# Revit family: 926-10-001-DN50-500
name_source: partatom
category: Pipe Accessories
units: mm (PartAtom-declared; Revit-internal decimal feet)

## family parameters
Always vertical = Yes
Cut with Voids When Loaded = No
Part Type = Valve - Breaks Into
Round Connector Dimension = Use Diameter
Shared = No
Work Plane-Based = No

## types (18) — shared parameters
DN050_PN 10/16 = 926-050-10-020140100000
DN080_PN 10/16 = 926-080-10-020140100000
DN100_PN 10/16 = 926-100-10-020140100000
DN150_PN 10/16 = 926-150-10-020040100000
DN200_PN 10 = 926-200-10-010040100000
DN200_PN 16 = 926-200-10-020040100000
DN250_PN 10 = 926-250-10-010040100000
DN250_PN 16 = 926-250-10-020040100000
DN300_PN 10 = 926-300-10-010040100000
DN300_PN 16 = 926-300-10-020040100000
DN350_PN 10 = 926-350-10-010040100000
DN350_PN 16 = 926-350-10-020040100000
DN400_PN 10 = 926-400-10-010040100000
DN400_PN 16 = 926-400-10-020040100000
DN450_PN 10 = 926-450-10-010040100000
DN450_PN 16 = 926-450-10-020040100000
DN500_PN 10 = 926-500-10-010040100000
DN500_PN 16 = 926-500-10-020040100000
Search_table = 926-10-001-DN50-500
URL_product_pages = https://www.avkvalves.com
zero-valued in all types: Default Elevation

## per-type parameters (varying)
- DN500_PN 16: A=130 mm; B=380 mm; Body_T=15 mm  [stored 0.0492126 ft]; Body_end_shaft_R=58 mm; Body_rib_L=87 mm; Body_rib_W=38 mm  [stored 0.124672 ft]; Body_shaft_R1=51 mm; Body_shaft_R2=44 mm; Body_shaft_R2_T=37 mm; Body_shaft_R3=57 mm; Body_shaft_R3_T=20 mm  [stored 0.0656168 ft]; Bore_R=250 mm; C=511 mm; D=46 mm; DN=500 mm; Description_=AVK DBL. ECC. BUTTERFLY VALVE, WAFER; E=65 mm; FL_R=285 mm; FL_T=22 mm  [stored 0.0721785 ft]; Hole_R=16 mm  [stored 0.0524934 ft]; L=6 mm  [stored 0.019685 ft]; PCD=650 mm; Raised_R=260 mm; Raised_dis=4 mm  [stored 0.0131234 ft]; Rib_R=23 mm  [stored 0.0754593 ft]; Rib_T=12 mm  [stored 0.0393701 ft]; Seal_R=18 mm  [stored 0.0590551 ft]; Slot_T=29 mm; Slot_dim1=12 mm  [stored 0.0393701 ft]; Top _Flange_dim1=38 mm  [stored 0.124672 ft]; Top _Flange_dim2=40 mm  [stored 0.131234 ft]; Top_Flange_R=105 mm; Top_Rib=23 mm  [stored 0.0754593 ft]; Wedge=100 mm; bottom_Shaft_R=59 mm; bottom_Shaft_T=27 mm  [stored 0.0885827 ft]; logo=267 mm; rib_Loctn=35 mm  [stored 0.114829 ft]; total_FL_legth=124 mm
- DN500_PN 10: A=130 mm; B=380 mm; Body_T=15 mm  [stored 0.0492126 ft]; Body_end_shaft_R=58 mm; Body_rib_L=87 mm; Body_rib_W=38 mm  [stored 0.124672 ft]; Body_shaft_R1=53 mm; Body_shaft_R2=44 mm; Body_shaft_R2_T=37 mm; Body_shaft_R3=57 mm; Body_shaft_R3_T=20 mm  [stored 0.0656168 ft]; Bore_R=250 mm; C=511 mm; D=46 mm; DN=500 mm; Description_=AVK DBL. ECC. BUTTERFLY VALVE, WAFER; E=65 mm; FL_R=285 mm; FL_T=19 mm  [stored 0.062336 ft]; Hole_R=16 mm  [stored 0.0524934 ft]; L=6 mm  [stored 0.019685 ft]; PCD=620 mm; Raised_R=260 mm; Raised_dis=4 mm  [stored 0.0131234 ft]; Rib_R=23 mm  [stored 0.0754593 ft]; Rib_T=10 mm  [stored 0.0328084 ft]; Seal_R=18 mm  [stored 0.0590551 ft]; Slot_T=29 mm; Slot_dim1=12 mm  [stored 0.0393701 ft]; Top _Flange_dim1=38 mm  [stored 0.124672 ft]; Top _Flange_dim2=40 mm  [stored 0.131234 ft]; Top_Flange_R=105 mm; Top_Rib=23 mm  [stored 0.0754593 ft]; Wedge=100 mm; bottom_Shaft_R=59 mm; bottom_Shaft_T=27 mm  [stored 0.0885827 ft]; logo=267 mm; rib_Loctn=35 mm  [stored 0.114829 ft]; total_FL_legth=124 mm
- DN450_PN 16: A=117 mm; B=360 mm; Body_T=16 mm  [stored 0.0524934 ft]; Body_end_shaft_R=52 mm; Body_rib_L=78 mm; Body_rib_W=41 mm  [stored 0.134514 ft]; Body_shaft_R1=45 mm; Body_shaft_R2=39 mm  [stored 0.127953 ft]; Body_shaft_R2_T=29 mm; Body_shaft_R3=51 mm; Body_shaft_R3_T=16 mm  [stored 0.0524934 ft]; Bore_R=225 mm; C=492 mm; D=36 mm  [stored 0.11811 ft]; DN=450 mm; Description_=AVK DBL. ECC. BUTTERFLY VALVE, WAFER; E=38 mm  [stored 0.124672 ft]; FL_R=265 mm; FL_T=22 mm  [stored 0.0721785 ft]; Hole_R=15 mm  [stored 0.0492126 ft]; L=6 mm  [stored 0.019685 ft]; PCD=585 mm; Raised_R=245 mm; Raised_dis=4 mm  [stored 0.0131234 ft]; Rib_R=18 mm  [stored 0.0590551 ft]; Rib_T=12 mm  [stored 0.0393701 ft]; Seal_R=20 mm  [stored 0.0656168 ft]; Slot_T=23 mm  [stored 0.0754593 ft]; Slot_dim1=10 mm  [stored 0.0328084 ft]; Top _Flange_dim1=34 mm  [stored 0.111549 ft]; Top _Flange_dim2=31 mm  [stored 0.101706 ft]; Top_Flange_R=105 mm; Top_Rib=18 mm  [stored 0.0590551 ft]; Wedge=90 mm; bottom_Shaft_R=53 mm; bottom_Shaft_T=29 mm; logo=243 mm; rib_Loctn=31 mm  [stored 0.101706 ft]; total_FL_legth=111 mm
- DN450_PN 10: A=117 mm; B=360 mm; Body_T=16 mm  [stored 0.0524934 ft]; Body_end_shaft_R=52 mm; Body_rib_L=78 mm; Body_rib_W=41 mm  [stored 0.134514 ft]; Body_shaft_R1=46 mm; Body_shaft_R2=39 mm  [stored 0.127953 ft]; Body_shaft_R2_T=29 mm; Body_shaft_R3=51 mm; Body_shaft_R3_T=16 mm  [stored 0.0524934 ft]; Bore_R=225 mm; C=492 mm; D=36 mm  [stored 0.11811 ft]; DN=450 mm; Description_=AVK DBL. ECC. BUTTERFLY VALVE, WAFER; E=38 mm  [stored 0.124672 ft]; FL_R=265 mm; FL_T=19 mm  [stored 0.062336 ft]; Hole_R=15 mm  [stored 0.0492126 ft]; L=6 mm  [stored 0.019685 ft]; PCD=565 mm; Raised_R=245 mm; Raised_dis=4 mm  [stored 0.0131234 ft]; Rib_R=18 mm  [stored 0.0590551 ft]; Rib_T=10 mm  [stored 0.0328084 ft]; Seal_R=20 mm  [stored 0.0656168 ft]; Slot_T=23 mm  [stored 0.0754593 ft]; Slot_dim1=10 mm  [stored 0.0328084 ft]; Top _Flange_dim1=34 mm  [stored 0.111549 ft]; Top _Flange_dim2=31 mm  [stored 0.101706 ft]; Top_Flange_R=105 mm; Top_Rib=18 mm  [stored 0.0590551 ft]; Wedge=90 mm; bottom_Shaft_R=53 mm; bottom_Shaft_T=29 mm; logo=243 mm; rib_Loctn=31 mm  [stored 0.101706 ft]; total_FL_legth=111 mm
- DN400_PN 16: A=105 mm; B=350 mm; Body_T=15 mm  [stored 0.0492126 ft]; Body_end_shaft_R=46 mm; Body_rib_L=70 mm; Body_rib_W=42 mm; Body_shaft_R1=39 mm  [stored 0.127953 ft]; Body_shaft_R2=35 mm  [stored 0.114829 ft]; Body_shaft_R2_T=29 mm; Body_shaft_R3=46 mm; Body_shaft_R3_T=16 mm  [stored 0.0524934 ft]; Bore_R=200 mm; C=451 mm; D=36 mm  [stored 0.11811 ft]; DN=400 mm; Description_=AVK DBL. ECC. BUTTERFLY VALVE, WAFER; E=41 mm  [stored 0.134514 ft]; FL_R=240 mm; FL_T=22 mm  [stored 0.0721785 ft]; Hole_R=14 mm  [stored 0.0459318 ft]; L=6 mm  [stored 0.019685 ft]; PCD=525 mm; Raised_R=220 mm; Raised_dis=4 mm  [stored 0.0131234 ft]; Rib_R=18 mm  [stored 0.0590551 ft]; Rib_T=12 mm  [stored 0.0393701 ft]; Seal_R=20 mm  [stored 0.0656168 ft]; Slot_T=23 mm  [stored 0.0754593 ft]; Slot_dim1=10 mm  [stored 0.0328084 ft]; Top _Flange_dim1=31 mm  [stored 0.101706 ft]; Top _Flange_dim2=31 mm  [stored 0.101706 ft]; Top_Flange_R=88 mm; Top_Rib=18 mm  [stored 0.0590551 ft]; Wedge=81 mm; bottom_Shaft_R=48 mm; bottom_Shaft_T=29 mm; logo=217 mm; rib_Loctn=28 mm  [stored 0.0918635 ft]; total_FL_legth=99 mm
- DN400_PN 10: A=51 mm; B=110 mm; Body_T=8 mm  [stored 0.0262467 ft]; Body_end_shaft_R=22 mm  [stored 0.0721785 ft]; Body_rib_L=20 mm  [stored 0.0656168 ft]; Body_rib_W=12 mm  [stored 0.0393701 ft]; Body_shaft_R1=19 mm  [stored 0.062336 ft]; Body_shaft_R2=10 mm  [stored 0.0328084 ft]; Body_shaft_R2_T=7 mm  [stored 0.0229659 ft]; Body_shaft_R3=13 mm; Body_shaft_R3_T=4 mm  [stored 0.0131234 ft]; Bore_R=40 mm  [stored 0.131234 ft]; C=185 mm; D=9 mm  [stored 0.0295276 ft]; DN=80 mm; Description_=AVK DBL. ECC. BUTTERFLY VALVE, WAFER AWWA SHORT, PN10/16; E=18 mm  [stored 0.0590551 ft]; FL_R=75 mm; FL_T=10 mm  [stored 0.0328084 ft]; Hole_R=5 mm  [stored 0.0164042 ft]; L=3 mm  [stored 0.00984252 ft]; PCD=160 mm; Raised_R=64 mm; Raised_dis=2 mm  [stored 0.00656168 ft]; Rib_R=5 mm  [stored 0.0164042 ft]; Rib_T=5 mm  [stored 0.0164042 ft]; Seal_R=18 mm  [stored 0.0590551 ft]; Slot_T=6 mm  [stored 0.019685 ft]; Slot_dim1=2 mm  [stored 0.00656168 ft]; Top _Flange_dim1=9 mm  [stored 0.0295276 ft]; Top _Flange_dim2=8 mm  [stored 0.0262467 ft]; Top_Flange_R=45 mm; Top_Rib=5 mm  [stored 0.0164042 ft]; Wedge=39 mm  [stored 0.127953 ft]; bottom_Shaft_R=14 mm  [stored 0.0459318 ft]; bottom_Shaft_T=8 mm  [stored 0.0262467 ft]; logo=50 mm; rib_Loctn=8 mm  [stored 0.0262467 ft]; total_FL_legth=48 mm
- DN350_PN 16: A=96 mm; B=290 mm; Body_T=14 mm  [stored 0.0459318 ft]; Body_end_shaft_R=43 mm; Body_rib_L=67 mm; Body_rib_W=31 mm  [stored 0.101706 ft]; Body_shaft_R1=36 mm  [stored 0.11811 ft]; Body_shaft_R2=34 mm  [stored 0.111549 ft]; Body_shaft_R2_T=29 mm; Body_shaft_R3=44 mm; Body_shaft_R3_T=16 mm  [stored 0.0524934 ft]; Bore_R=175 mm; C=420 mm; D=36 mm  [stored 0.11811 ft]; DN=350 mm; Description_=AVK DBL. ECC. BUTTERFLY VALVE, WAFER; E=41 mm  [stored 0.134514 ft]; FL_R=210 mm; FL_T=20 mm  [stored 0.0656168 ft]; Hole_R=13 mm; L=5 mm  [stored 0.0164042 ft]; PCD=470 mm; Raised_R=190 mm; Raised_dis=3 mm  [stored 0.00984252 ft]; Rib_R=18 mm  [stored 0.0590551 ft]; Rib_T=11 mm  [stored 0.0360892 ft]; Seal_R=18 mm  [stored 0.0590551 ft]; Slot_T=23 mm  [stored 0.0754593 ft]; Slot_dim1=10 mm  [stored 0.0328084 ft]; Top _Flange_dim1=30 mm  [stored 0.0984252 ft]; Top _Flange_dim2=31 mm  [stored 0.101706 ft]; Top_Flange_R=75 mm; Top_Rib=18 mm  [stored 0.0590551 ft]; Wedge=74 mm; bottom_Shaft_R=46 mm; bottom_Shaft_T=22 mm  [stored 0.0721785 ft]; logo=191 mm; rib_Loctn=27 mm  [stored 0.0885827 ft]; total_FL_legth=92 mm
- DN350_PN 10: A=96 mm; B=290 mm; Body_T=14 mm  [stored 0.0459318 ft]; Body_end_shaft_R=43 mm; Body_rib_L=67 mm; Body_rib_W=31 mm  [stored 0.101706 ft]; Body_shaft_R1=37 mm; Body_shaft_R2=34 mm  [stored 0.111549 ft]; Body_shaft_R2_T=29 mm; Body_shaft_R3=44 mm; Body_shaft_R3_T=16 mm  [stored 0.0524934 ft]; Bore_R=175 mm; C=420 mm; D=36 mm  [stored 0.11811 ft]; DN=350 mm; Description_=AVK DBL. ECC. BUTTERFLY VALVE, WAFER; E=41 mm  [stored 0.134514 ft]; FL_R=210 mm; FL_T=18 mm  [stored 0.0590551 ft]; Hole_R=13 mm; L=5 mm  [stored 0.0164042 ft]; PCD=460 mm; Raised_R=190 mm; Raised_dis=3 mm  [stored 0.00984252 ft]; Rib_R=18 mm  [stored 0.0590551 ft]; Rib_T=10 mm  [stored 0.0328084 ft]; Seal_R=18 mm  [stored 0.0590551 ft]; Slot_T=23 mm  [stored 0.0754593 ft]; Slot_dim1=10 mm  [stored 0.0328084 ft]; Top _Flange_dim1=30 mm  [stored 0.0984252 ft]; Top _Flange_dim2=31 mm  [stored 0.101706 ft]; Top_Flange_R=75 mm; Top_Rib=18 mm  [stored 0.0590551 ft]; Wedge=74 mm; bottom_Shaft_R=46 mm; bottom_Shaft_T=22 mm  [stored 0.0721785 ft]; logo=191 mm; rib_Loctn=27 mm  [stored 0.0885827 ft]; total_FL_legth=92 mm
- DN300_PN 16: A=86 mm; B=260 mm; Body_T=14 mm  [stored 0.0459318 ft]; Body_end_shaft_R=38 mm  [stored 0.124672 ft]; Body_rib_L=60 mm; Body_rib_W=30 mm  [stored 0.0984252 ft]; Body_shaft_R1=32 mm  [stored 0.104987 ft]; Body_shaft_R2=30 mm  [stored 0.0984252 ft]; Body_shaft_R2_T=22 mm  [stored 0.0721785 ft]; Body_shaft_R3=39 mm  [stored 0.127953 ft]; Body_shaft_R3_T=12 mm  [stored 0.0393701 ft]; Bore_R=150 mm; C=390 mm; D=27 mm  [stored 0.0885827 ft]; DN=300 mm; Description_=AVK DBL. ECC. BUTTERFLY VALVE, WAFER; E=41 mm  [stored 0.134514 ft]; FL_R=180 mm; FL_T=18 mm  [stored 0.0590551 ft]; Hole_R=12 mm  [stored 0.0393701 ft]; L=5 mm  [stored 0.0164042 ft]; PCD=410 mm; Raised_R=160 mm; Raised_dis=3 mm  [stored 0.00984252 ft]; Rib_R=14 mm  [stored 0.0459318 ft]; Rib_T=10 mm  [stored 0.0328084 ft]; Seal_R=15 mm  [stored 0.0492126 ft]; Slot_T=17 mm  [stored 0.0557743 ft]; Slot_dim1=7 mm  [stored 0.0229659 ft]; Top _Flange_dim1=27 mm  [stored 0.0885827 ft]; Top _Flange_dim2=23 mm  [stored 0.0754593 ft]; Top_Flange_R=75 mm; Top_Rib=14 mm  [stored 0.0459318 ft]; Wedge=66 mm; bottom_Shaft_R=41 mm  [stored 0.134514 ft]; bottom_Shaft_T=21 mm  [stored 0.0688976 ft]; logo=166 mm; rib_Loctn=24 mm  [stored 0.0787402 ft]; total_FL_legth=81 mm
- DN300_PN 10: A=86 mm; B=260 mm; Body_T=14 mm  [stored 0.0459318 ft]; Body_end_shaft_R=38 mm  [stored 0.124672 ft]; Body_rib_L=60 mm; Body_rib_W=30 mm  [stored 0.0984252 ft]; Body_shaft_R1=32 mm  [stored 0.104987 ft]; Body_shaft_R2=30 mm  [stored 0.0984252 ft]; Body_shaft_R2_T=22 mm  [stored 0.0721785 ft]; Body_shaft_R3=39 mm  [stored 0.127953 ft]; Body_shaft_R3_T=12 mm  [stored 0.0393701 ft]; Bore_R=150 mm; C=390 mm; D=27 mm  [stored 0.0885827 ft]; DN=300 mm; Description_=AVK DBL. ECC. BUTTERFLY VALVE, WAFER; E=41 mm  [stored 0.134514 ft]; FL_R=180 mm; FL_T=18 mm  [stored 0.0590551 ft]; Hole_R=12 mm  [stored 0.0393701 ft]; L=5 mm  [stored 0.0164042 ft]; PCD=400 mm; Raised_R=160 mm; Raised_dis=3 mm  [stored 0.00984252 ft]; Rib_R=14 mm  [stored 0.0459318 ft]; Rib_T=10 mm  [stored 0.0328084 ft]; Seal_R=15 mm  [stored 0.0492126 ft]; Slot_T=17 mm  [stored 0.0557743 ft]; Slot_dim1=7 mm  [stored 0.0229659 ft]; Top _Flange_dim1=27 mm  [stored 0.0885827 ft]; Top _Flange_dim2=23 mm  [stored 0.0754593 ft]; Top_Flange_R=75 mm; Top_Rib=14 mm  [stored 0.0459318 ft]; Wedge=66 mm; bottom_Shaft_R=41 mm  [stored 0.134514 ft]; bottom_Shaft_T=21 mm  [stored 0.0688976 ft]; logo=166 mm; rib_Loctn=24 mm  [stored 0.0787402 ft]; total_FL_legth=81 mm
- DN250_PN 16: A=79 mm; B=222 mm; Body_T=4 mm  [stored 0.0131234 ft]; Body_end_shaft_R=36 mm  [stored 0.11811 ft]; Body_rib_L=56 mm; Body_rib_W=24 mm  [stored 0.0787402 ft]; Body_shaft_R1=29 mm; Body_shaft_R2=28 mm  [stored 0.0918635 ft]; Body_shaft_R2_T=22 mm  [stored 0.0721785 ft]; Body_shaft_R3=36 mm  [stored 0.11811 ft]; Body_shaft_R3_T=12 mm  [stored 0.0393701 ft]; Bore_R=125 mm; C=340 mm; D=27 mm  [stored 0.0885827 ft]; DN=250 mm; Description_=AVK DBL. ECC. BUTTERFLY VALVE, WAFER; E=36 mm  [stored 0.11811 ft]; FL_R=160 mm; FL_T=18 mm  [stored 0.0590551 ft]; Hole_R=11 mm  [stored 0.0360892 ft]; L=3 mm  [stored 0.00984252 ft]; PCD=350 mm; Raised_R=140 mm; Raised_dis=2 mm  [stored 0.00656168 ft]; Rib_R=14 mm  [stored 0.0459318 ft]; Rib_T=11 mm  [stored 0.0360892 ft]; Seal_R=18 mm  [stored 0.0590551 ft]; Slot_T=17 mm  [stored 0.0557743 ft]; Slot_dim1=7 mm  [stored 0.0229659 ft]; Top _Flange_dim1=25 mm  [stored 0.082021 ft]; Top _Flange_dim2=23 mm  [stored 0.0754593 ft]; Top_Flange_R=75 mm; Top_Rib=14 mm  [stored 0.0459318 ft]; Wedge=61 mm; bottom_Shaft_R=38 mm  [stored 0.124672 ft]; bottom_Shaft_T=17 mm  [stored 0.0557743 ft]; logo=131 mm; rib_Loctn=22 mm  [stored 0.0721785 ft]; total_FL_legth=76 mm
- DN250_PN 10: A=79 mm; B=222 mm; Body_T=14 mm  [stored 0.0459318 ft]; Body_end_shaft_R=36 mm  [stored 0.11811 ft]; Body_rib_L=56 mm; Body_rib_W=24 mm  [stored 0.0787402 ft]; Body_shaft_R1=29 mm; Body_shaft_R2=28 mm  [stored 0.0918635 ft]; Body_shaft_R2_T=22 mm  [stored 0.0721785 ft]; Body_shaft_R3=36 mm  [stored 0.11811 ft]; Body_shaft_R3_T=12 mm  [stored 0.0393701 ft]; Bore_R=125 mm; C=340 mm; D=27 mm  [stored 0.0885827 ft]; DN=250 mm; Description_=AVK DBL. ECC. BUTTERFLY VALVE, WAFER; E=36 mm  [stored 0.11811 ft]; FL_R=160 mm; FL_T=18 mm  [stored 0.0590551 ft]; Hole_R=11 mm  [stored 0.0360892 ft]; L=3 mm  [stored 0.00984252 ft]; PCD=350 mm; Raised_R=140 mm; Raised_dis=2 mm  [stored 0.00656168 ft]; Rib_R=14 mm  [stored 0.0459318 ft]; Rib_T=11 mm  [stored 0.0360892 ft]; Seal_R=18 mm  [stored 0.0590551 ft]; Slot_T=17 mm  [stored 0.0557743 ft]; Slot_dim1=7 mm  [stored 0.0229659 ft]; Top _Flange_dim1=25 mm  [stored 0.082021 ft]; Top _Flange_dim2=23 mm  [stored 0.0754593 ft]; Top_Flange_R=75 mm; Top_Rib=14 mm  [stored 0.0459318 ft]; Wedge=61 mm; bottom_Shaft_R=38 mm  [stored 0.124672 ft]; bottom_Shaft_T=17 mm  [stored 0.0557743 ft]; logo=141 mm; rib_Loctn=22 mm  [stored 0.0721785 ft]; total_FL_legth=76 mm
- DN200_PN 16: A=75 mm; B=200 mm; Body_T=14 mm  [stored 0.0459318 ft]; Body_end_shaft_R=34 mm  [stored 0.111549 ft]; Body_rib_L=52 mm; Body_rib_W=22 mm  [stored 0.0721785 ft]; Body_shaft_R1=27 mm  [stored 0.0885827 ft]; Body_shaft_R2=26 mm; Body_shaft_R2_T=18 mm  [stored 0.0590551 ft]; Body_shaft_R3=34 mm  [stored 0.111549 ft]; Body_shaft_R3_T=10 mm  [stored 0.0328084 ft]; Bore_R=100 mm; C=320 mm; D=22 mm  [stored 0.0721785 ft]; DN=200 mm; Description_=AVK DBL. ECC. BUTTERFLY VALVE, WAFER; E=30 mm  [stored 0.0984252 ft]; FL_R=130 mm; FL_T=17 mm  [stored 0.0557743 ft]; Hole_R=10 mm  [stored 0.0328084 ft]; L=3 mm  [stored 0.00984252 ft]; PCD=295 mm; Raised_R=110 mm; Raised_dis=2 mm  [stored 0.00656168 ft]; Rib_R=11 mm  [stored 0.0360892 ft]; Rib_T=10 mm  [stored 0.0328084 ft]; Seal_R=15 mm  [stored 0.0492126 ft]; Slot_T=14 mm  [stored 0.0459318 ft]; Slot_dim1=6 mm  [stored 0.019685 ft]; Top _Flange_dim1=23 mm  [stored 0.0754593 ft]; Top _Flange_dim2=19 mm  [stored 0.062336 ft]; Top_Flange_R=63 mm; Top_Rib=11 mm  [stored 0.0360892 ft]; Wedge=57 mm; bottom_Shaft_R=35 mm  [stored 0.114829 ft]; bottom_Shaft_T=15 mm  [stored 0.0492126 ft]; logo=116 mm; rib_Loctn=21 mm  [stored 0.0688976 ft]; total_FL_legth=72 mm
- DN200_PN 10: A=75 mm; B=200 mm; Body_T=12 mm  [stored 0.0393701 ft]; Body_end_shaft_R=34 mm  [stored 0.111549 ft]; Body_rib_L=52 mm; Body_rib_W=22 mm  [stored 0.0721785 ft]; Body_shaft_R1=28 mm  [stored 0.0918635 ft]; Body_shaft_R2=26 mm; Body_shaft_R2_T=18 mm  [stored 0.0590551 ft]; Body_shaft_R3=34 mm  [stored 0.111549 ft]; Body_shaft_R3_T=10 mm  [stored 0.0328084 ft]; Bore_R=100 mm; C=320 mm; D=22 mm  [stored 0.0721785 ft]; DN=200 mm; Description_=AVK DBL. ECC. BUTTERFLY VALVE, WAFER; E=30 mm  [stored 0.0984252 ft]; FL_R=130 mm; FL_T=15 mm  [stored 0.0492126 ft]; Hole_R=10 mm  [stored 0.0328084 ft]; L=3 mm  [stored 0.00984252 ft]; PCD=295 mm; Raised_R=110 mm; Raised_dis=2 mm  [stored 0.00656168 ft]; Rib_R=11 mm  [stored 0.0360892 ft]; Rib_T=9 mm  [stored 0.0295276 ft]; Seal_R=15 mm  [stored 0.0492126 ft]; Slot_T=14 mm  [stored 0.0459318 ft]; Slot_dim1=6 mm  [stored 0.019685 ft]; Top _Flange_dim1=23 mm  [stored 0.0754593 ft]; Top _Flange_dim2=19 mm  [stored 0.062336 ft]; Top_Flange_R=63 mm; Top_Rib=11 mm  [stored 0.0360892 ft]; Wedge=57 mm; bottom_Shaft_R=35 mm  [stored 0.114829 ft]; bottom_Shaft_T=15 mm  [stored 0.0492126 ft]; logo=114 mm; rib_Loctn=21 mm  [stored 0.0688976 ft]; total_FL_legth=72 mm
- DN150_PN 10/16: A=71 mm; B=170 mm; Body_T=12 mm  [stored 0.0393701 ft]; Body_end_shaft_R=32 mm  [stored 0.104987 ft]; Body_rib_L=32 mm  [stored 0.104987 ft]; Body_rib_W=20 mm  [stored 0.0656168 ft]; Body_shaft_R1=28 mm  [stored 0.0918635 ft]; Body_shaft_R2=16 mm  [stored 0.0524934 ft]; Body_shaft_R2_T=14 mm  [stored 0.0459318 ft]; Body_shaft_R3=21 mm  [stored 0.0688976 ft]; Body_shaft_R3_T=7 mm  [stored 0.0229659 ft]; Bore_R=75 mm; C=280 mm; D=17 mm  [stored 0.0557743 ft]; DN=150 mm; Description_=AVK DBL. ECC. BUTTERFLY VALVE, WAFER; E=27 mm  [stored 0.0885827 ft]; FL_R=102 mm; FL_T=13 mm; Hole_R=8 mm  [stored 0.0262467 ft]; L=3 mm  [stored 0.00984252 ft]; PCD=240 mm; Raised_R=90 mm; Raised_dis=2 mm  [stored 0.00656168 ft]; Rib_R=9 mm  [stored 0.0295276 ft]; Rib_T=7 mm  [stored 0.0229659 ft]; Seal_R=14 mm  [stored 0.0459318 ft]; Slot_T=11 mm  [stored 0.0360892 ft]; Slot_dim1=5 mm  [stored 0.0164042 ft]; Top _Flange_dim1=14 mm  [stored 0.0459318 ft]; Top _Flange_dim2=15 mm  [stored 0.0492126 ft]; Top_Flange_R=63 mm; Top_Rib=9 mm  [stored 0.0295276 ft]; Wedge=55 mm; bottom_Shaft_R=22 mm  [stored 0.0721785 ft]; bottom_Shaft_T=14 mm  [stored 0.0459318 ft]; logo=89 mm; rib_Loctn=13 mm; total_FL_legth=68 mm
- DN100_PN 10/16: A=57 mm; B=130 mm; Body_T=10 mm  [stored 0.0328084 ft]; Body_end_shaft_R=25 mm  [stored 0.082021 ft]; Body_rib_L=25 mm  [stored 0.082021 ft]; Body_rib_W=15 mm  [stored 0.0492126 ft]; Body_shaft_R1=22 mm  [stored 0.0721785 ft]; Body_shaft_R2=13 mm; Body_shaft_R2_T=9 mm  [stored 0.0295276 ft]; Body_shaft_R3=16 mm  [stored 0.0524934 ft]; Body_shaft_R3_T=5 mm  [stored 0.0164042 ft]; Bore_R=50 mm; C=202 mm; D=11 mm  [stored 0.0360892 ft]; DN=100 mm; Description_=AVK DBL. ECC. BUTTERFLY VALVE, WAFER; E=20 mm  [stored 0.0656168 ft]; FL_R=82 mm; FL_T=11 mm  [stored 0.0360892 ft]; Hole_R=6 mm  [stored 0.019685 ft]; L=3 mm  [stored 0.00984252 ft]; PCD=180 mm; Raised_R=65 mm; Raised_dis=2 mm  [stored 0.00656168 ft]; Rib_R=6 mm  [stored 0.019685 ft]; Rib_T=6 mm  [stored 0.019685 ft]; Seal_R=16 mm  [stored 0.0524934 ft]; Slot_T=7 mm  [stored 0.0229659 ft]; Slot_dim1=3 mm  [stored 0.00984252 ft]; Top _Flange_dim1=11 mm  [stored 0.0360892 ft]; Top _Flange_dim2=10 mm  [stored 0.0328084 ft]; Top_Flange_R=45 mm; Top_Rib=6 mm  [stored 0.019685 ft]; Wedge=44 mm; bottom_Shaft_R=17 mm  [stored 0.0557743 ft]; bottom_Shaft_T=11 mm  [stored 0.0360892 ft]; logo=62 mm; rib_Loctn=10 mm  [stored 0.0328084 ft]; total_FL_legth=54 mm
- DN080_PN 10/16: A=51 mm; B=80 mm; Body_T=8 mm  [stored 0.0262467 ft]; Body_end_shaft_R=22 mm  [stored 0.0721785 ft]; Body_rib_L=15 mm  [stored 0.0492126 ft]; Body_rib_W=8 mm  [stored 0.0262467 ft]; Body_shaft_R1=19 mm  [stored 0.062336 ft]; Body_shaft_R2=8 mm  [stored 0.0262467 ft]; Body_shaft_R2_T=7 mm  [stored 0.0229659 ft]; Body_shaft_R3=10 mm  [stored 0.0328084 ft]; Body_shaft_R3_T=4 mm  [stored 0.0131234 ft]; Bore_R=25 mm  [stored 0.082021 ft]; C=110 mm; D=9 mm  [stored 0.0295276 ft]; DN=50 mm; Description_=AVK DBL. ECC. BUTTERFLY VALVE, WAFER; E=18 mm  [stored 0.0590551 ft]; FL_R=52 mm; FL_T=10 mm  [stored 0.0328084 ft]; Hole_R=4 mm  [stored 0.0131234 ft]; L=3 mm  [stored 0.00984252 ft]; PCD=120 mm; Raised_R=34 mm  [stored 0.111549 ft]; Raised_dis=2 mm  [stored 0.00656168 ft]; Rib_R=5 mm  [stored 0.0164042 ft]; Rib_T=5 mm  [stored 0.0164042 ft]; Seal_R=14 mm  [stored 0.0459318 ft]; Slot_T=6 mm  [stored 0.019685 ft]; Slot_dim1=2 mm  [stored 0.00656168 ft]; Top _Flange_dim1=7 mm  [stored 0.0229659 ft]; Top _Flange_dim2=8 mm  [stored 0.0262467 ft]; Top_Flange_R=45 mm; Top_Rib=5 mm  [stored 0.0164042 ft]; Wedge=39 mm  [stored 0.127953 ft]; bottom_Shaft_R=10 mm  [stored 0.0328084 ft]; bottom_Shaft_T=6 mm  [stored 0.019685 ft]; logo=35 mm  [stored 0.114829 ft]; rib_Loctn=6 mm  [stored 0.019685 ft]; total_FL_legth=48 mm
- DN050_PN 10/16: A=86 mm; B=260 mm; Body_T=14 mm  [stored 0.0459318 ft]; Body_end_shaft_R=38 mm  [stored 0.124672 ft]; Body_rib_L=60 mm; Body_rib_W=30 mm  [stored 0.0984252 ft]; Body_shaft_R1=32 mm  [stored 0.104987 ft]; Body_shaft_R2=30 mm  [stored 0.0984252 ft]; Body_shaft_R2_T=22 mm  [stored 0.0721785 ft]; Body_shaft_R3=39 mm  [stored 0.127953 ft]; Body_shaft_R3_T=12 mm  [stored 0.0393701 ft]; Bore_R=150 mm; C=390 mm; D=27 mm  [stored 0.0885827 ft]; DN=300 mm; Description_=AVK DBL. ECC. BUTTERFLY VALVE, WAFER; E=41 mm  [stored 0.134514 ft]; FL_R=180 mm; FL_T=18 mm  [stored 0.0590551 ft]; Hole_R=12 mm  [stored 0.0393701 ft]; L=5 mm  [stored 0.0164042 ft]; PCD=400 mm; Raised_R=160 mm; Raised_dis=3 mm  [stored 0.00984252 ft]; Rib_R=14 mm  [stored 0.0459318 ft]; Rib_T=10 mm  [stored 0.0328084 ft]; Seal_R=15 mm  [stored 0.0492126 ft]; Slot_T=17 mm  [stored 0.0557743 ft]; Slot_dim1=7 mm  [stored 0.0229659 ft]; Top _Flange_dim1=27 mm  [stored 0.0885827 ft]; Top _Flange_dim2=23 mm  [stored 0.0754593 ft]; Top_Flange_R=75 mm; Top_Rib=14 mm  [stored 0.0459318 ft]; Wedge=66 mm; bottom_Shaft_R=41 mm  [stored 0.134514 ft]; bottom_Shaft_T=21 mm  [stored 0.0688976 ft]; logo=166 mm; rib_Loctn=24 mm  [stored 0.0787402 ft]; total_FL_legth=81 mm

note: [stored X ft] marks values corroborated as IEEE doubles in the binary element streams (Revit-internal decimal feet)

## geometry (parser evidence)
native form markers: Sweep x10
no freeform markers — native parametric forms only
